# Revit family: Amplifier-Power-Q-SYS-Networkable-SPA-Qf-4 Channel-Single
name_source: partatom
category: Communication Devices
units: mm (PartAtom-declared; Revit-internal decimal feet)

## family parameters
Cut with Voids When Loaded = No
Host = Face
Maintain Annotation Orientation = No
OmniClass Number = 23.85.10.14
OmniClass Title = Visual Information Systems
Part Type = Normal
Room Calculation Point = No
Round Connector Dimension = Use Diameter
Shared = No

## types (2) — shared parameters
Apparent Load = 1000 VA
Body Height = 30.5 mm  [stored 0.100066 ft]
Body Material = Paint - Q-SYS - Black
Body Width = 446 mm  [stored 1.46325 ft]
Bracket Depth = 80 mm  [stored 0.262467 ft]
Default Elevation = 1219.2 mm  [stored 4 ft]
Depth = 287 mm  [stored 0.941601 ft]
Description = Single network amplifier for Q-SYS platform
Frame Depth = 2 mm  [stored 0.00656168 ft]
Frame Height = 30.5 mm  [stored 0.100066 ft]
Grille Material = Paint - Q-SYS - Black Mesh
Height = 44 mm  [stored 0.144357 ft]
Highlight Material = Plastic - Q-SYS - Black
IQ Category = Amplifier
LED Material = Plastic - Q-SYS - LED Blue
Length 1 = 18.5 mm  [stored 0.0606955 ft]
Length 3 = 3 mm  [stored 0.00984252 ft]
Load Classification = Other
Manufacturer = Q-SYS
Manufacturer URL = https://www.qsys.com
Minimum Circuit Amps = 12 A
Model = SPA-Qf
Number of Poles = 2
Power Factor = 0.9
Product Documentation Link = https://www.qsys.com
Product Page URL = https://www.qsys.com
URL = https://www.qsys.com
Voltage = 75 V
Weight = 6.40 lbm
Weight Dimensional = 6.4
Weight Product = 6.4
Width = 483 mm  [stored 1.58465 ft]
zero-valued in all types: Body Offset

## per-type parameters (varying)
| type | Length 2 | Length 4 | Length 5 | Type Comments |
| Left Mount | 0 mm  [stored 0 ft] | 20 mm  [stored 0.0656168 ft] | 237 mm  [stored 0.777559 ft] | 4 Channel Left Mounted |
| Right Mount | 220 mm  [stored 0.721785 ft] | 237 mm  [stored 0.777559 ft] | 20 mm  [stored 0.0656168 ft] | 4 Channel Right Mounted |

type visibility flags: 2 boolean params named "<type name>" — each type sets only its own to Yes (folded from table)

note: [stored X ft] marks values corroborated as IEEE doubles in the binary element streams (Revit-internal decimal feet)

## geometry (parser evidence)
native form markers: Sweep x5
no freeform markers — native parametric forms only
